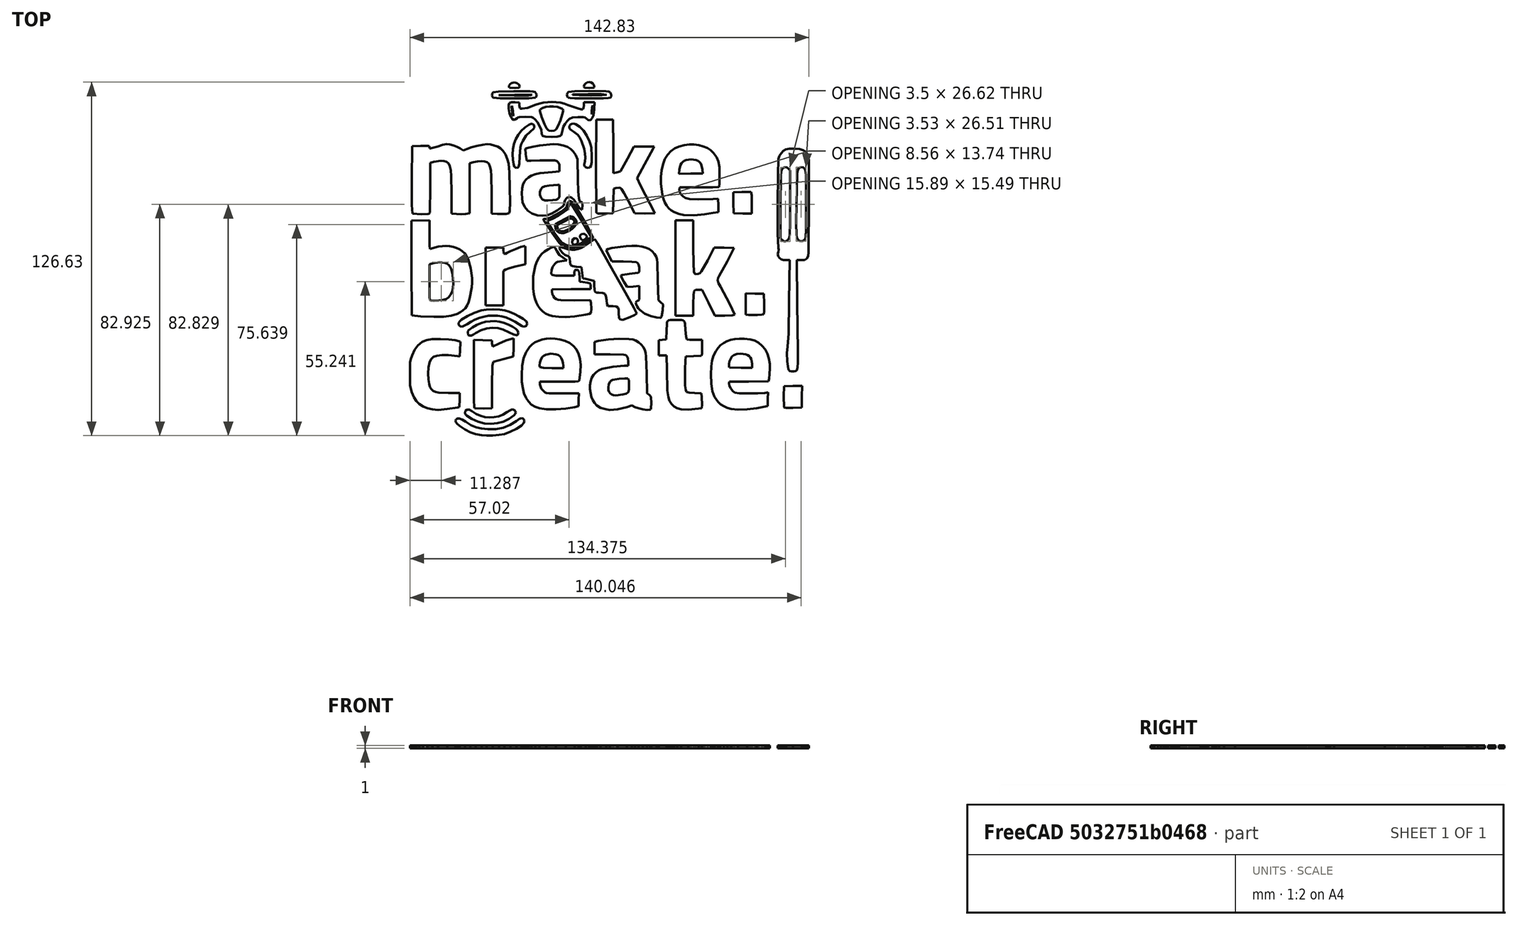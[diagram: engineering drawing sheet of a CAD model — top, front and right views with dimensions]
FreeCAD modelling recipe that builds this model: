
FCSTD DOCUMENT  (FreeCAD 1.0R39285 (Git))
Label: make_break_create_3d_01
License: All rights reserved
LicenseURL: http://www.ohwr.org/attachments/2388/cern_ohl_v_1_2.txt
objects: Part::Feature×50, Part::Extrusion×50, Part::Cut×12, Part::MultiFuse×2
note: 114 computed .brp shape members not serialized (recipe doc carries the construction recipe); baked Part::Feature solids carry a one-line shape summary decoded from their .brp

FEATURE [Part::Feature] Face
  shape: bbox 24.67 x 6.241 x 2e-07 mm, 1 faces, 0 solids (baked)
FEATURE [Part::Feature] Face001
  shape: bbox 18.26 x 5.149 x 2e-07 mm, 1 faces, 0 solids (baked)
FEATURE [Part::Feature] Face002
  shape: bbox 18.08 x 25.45 x 2e-07 mm, 1 faces, 0 solids (baked)
FEATURE [Part::Feature] Face003
  shape: bbox 21.9 x 25.59 x 2e-07 mm, 1 faces, 0 solids (baked)
FEATURE [Part::Feature] Face004
  shape: bbox 7.408 x 6.013 x 2e-07 mm, 1 faces, 0 solids (baked)
FEATURE [Part::Feature] Face005
  shape: bbox 21.11 x 25.45 x 2e-07 mm, 1 faces, 0 solids (baked)
FEATURE [Part::Feature] Face006
  shape: bbox 8.323 x 5.061 x 2e-07 mm, 1 faces, 0 solids (baked)
FEATURE [Part::Feature] Face007
  shape: bbox 15.61 x 32.1 x 2e-07 mm, 1 faces, 0 solids (baked)
FEATURE [Part::Feature] Face008
  shape: bbox 21.08 x 25.35 x 2e-07 mm, 1 faces, 0 solids (baked)
FEATURE [Part::Feature] Face009
  shape: bbox 8.448 x 5.165 x 2e-07 mm, 1 faces, 0 solids (baked)
FEATURE [Part::Feature] Face010
  shape: bbox 14.3 x 25.07 x 2e-07 mm, 1 faces, 0 solids (baked)
FEATURE [Part::Feature] Face011
  shape: bbox 6.571 x 7.896 x 2e-07 mm, 1 faces, 0 solids (baked)
FEATURE [Part::Feature] Face012
  shape: bbox 11.21 x 79.76 x 2e-07 mm, 1 faces, 0 solids (baked)
FEATURE [Part::Feature] Face013
  shape: bbox 3.498 x 26.62 x 2e-07 mm, 1 faces, 0 solids (baked)
FEATURE [Part::Feature] Face014
  shape: bbox 3.533 x 26.51 x 2e-07 mm, 1 faces, 0 solids (baked)
FEATURE [Part::Feature] Face015
  shape: bbox 17.99 x 5.158 x 2e-07 mm, 1 faces, 0 solids (baked)
FEATURE [Part::Feature] Face016
  shape: bbox 24.48 x 6.208 x 2e-07 mm, 1 faces, 0 solids (baked)
FEATURE [Part::Feature] Face017
  shape: bbox 27.63 x 28.88 x 2e-07 mm, 1 faces, 0 solids (baked)
FEATURE [Part::Feature] Face018
  shape: bbox 20.28 x 25.76 x 2e-07 mm, 1 faces, 0 solids (baked)
FEATURE [Part::Feature] Face019
  shape: bbox 21.72 x 34.62 x 2e-07 mm, 1 faces, 0 solids (baked)
FEATURE [Part::Feature] Face020
  shape: bbox 8.56 x 13.74 x 2e-07 mm, 1 faces, 0 solids (baked)
FEATURE [Part::Feature] Face021
  shape: bbox 20.87 x 25.1 x 2e-07 mm, 1 faces, 0 solids (baked)
FEATURE [Part::Feature] Face022
  shape: bbox 21.17 x 34.13 x 2e-07 mm, 1 faces, 0 solids (baked)
FEATURE [Part::Feature] Face023
  shape: bbox 6.556 x 7.79 x 2e-07 mm, 1 faces, 0 solids (baked)
FEATURE [Part::Feature] Face024
  shape: bbox 14.23 x 21.17 x 2e-07 mm, 1 faces, 0 solids (baked)
FEATURE [Part::Feature] Face025
  shape: bbox 17.77 x 16.59 x 2e-07 mm, 1 faces, 0 solids (baked)
FEATURE [Part::Feature] Face026
  shape: bbox 15.89 x 15.49 x 2e-07 mm, 1 faces, 0 solids (baked)
FEATURE [Part::Feature] Face027
  shape: bbox 2.125 x 2.325 x 2e-07 mm, 1 faces, 0 solids (baked)
FEATURE [Part::Feature] Face028
  shape: bbox 2.507 x 2.314 x 2e-07 mm, 1 faces, 0 solids (baked)
FEATURE [Part::Feature] Face029
  shape: bbox 7.664 x 6.077 x 2e-07 mm, 1 faces, 0 solids (baked)
FEATURE [Part::Feature] Face030
  shape: bbox 6.04 x 4.588 x 2e-07 mm, 1 faces, 0 solids (baked)
FEATURE [Part::Feature] Face031
  shape: bbox 21.68 x 25.65 x 2e-07 mm, 1 faces, 0 solids (baked)
FEATURE [Part::Feature] Face032
  shape: bbox 7.013 x 5.604 x 2e-07 mm, 1 faces, 0 solids (baked)
FEATURE [Part::Feature] Face033
  shape: bbox 20.97 x 25.39 x 2e-07 mm, 1 faces, 0 solids (baked)
FEATURE [Part::Feature] Face034
  shape: bbox 8.401 x 5.128 x 2e-07 mm, 1 faces, 0 solids (baked)
FEATURE [Part::Feature] Face035
  shape: bbox 35.11 x 25.08 x 2e-07 mm, 1 faces, 0 solids (baked)
FEATURE [Part::Feature] Face036
  shape: bbox 21.11 x 33.68 x 2e-07 mm, 1 faces, 0 solids (baked)
FEATURE [Part::Feature] Face037
  shape: bbox 6.615 x 7.752 x 2e-07 mm, 1 faces, 0 solids (baked)
FEATURE [Part::Feature] Face038
  shape: bbox 7.78 x 15.77 x 2e-07 mm, 1 faces, 0 solids (baked)
FEATURE [Part::Feature] Face039
  shape: bbox 7.999 x 15.82 x 2e-07 mm, 1 faces, 0 solids (baked)
FEATURE [Part::Feature] Face040
  shape: bbox 30.72 x 12.5 x 2e-07 mm, 1 faces, 0 solids (baked)
FEATURE [Part::Feature] Face041
  shape: bbox 8.329 x 8.723 x 2e-07 mm, 1 faces, 0 solids (baked)
FEATURE [Part::Feature] Face042
  shape: bbox 0.6332 x 3.652 x 2e-07 mm, 1 faces, 0 solids (baked)
FEATURE [Part::Feature] Face043
  shape: bbox 0.3788 x 3.244 x 2e-07 mm, 1 faces, 0 solids (baked)
FEATURE [Part::Feature] Face044
  shape: bbox 15.91 x 2.597 x 2e-07 mm, 1 faces, 0 solids (baked)
FEATURE [Part::Feature] Face045
  shape: bbox 11.85 x 0.339 x 2e-07 mm, 1 faces, 0 solids (baked)
FEATURE [Part::Feature] Face046
  shape: bbox 15.85 x 2.668 x 2e-07 mm, 1 faces, 0 solids (baked)
FEATURE [Part::Feature] Face047
  shape: bbox 12.2 x 0.4689 x 2e-07 mm, 1 faces, 0 solids (baked)
FEATURE [Part::Feature] Face048
  shape: bbox 3.826 x 1.977 x 2e-07 mm, 1 faces, 0 solids (baked)
FEATURE [Part::Feature] Face049
  shape: bbox 3.704 x 2.117 x 2e-07 mm, 1 faces, 0 solids (baked)
FEATURE [Part::Extrusion] Extrude
  Base = -> Face
  Dir = (0,0,-1)
  DirMode = 2
  FaceMakerClass = Part::FaceMakerBullseye
  FaceMakerMode = 3
  LengthFwd = 1
  LengthRev = 0
  Solid = false
  Symmetric = false
FEATURE [Part::Extrusion] Extrude001
  Base = -> Face001
  Dir = (0,0,-1)
  DirMode = 2
  FaceMakerClass = Part::FaceMakerBullseye
  FaceMakerMode = 3
  LengthFwd = 1
  LengthRev = 0
  Solid = false
  Symmetric = false
FEATURE [Part::Extrusion] Extrude002
  Base = -> Face002
  Dir = (0,0,-1)
  DirMode = 2
  FaceMakerClass = Part::FaceMakerBullseye
  FaceMakerMode = 3
  LengthFwd = 1
  LengthRev = 0
  Solid = false
  Symmetric = false
FEATURE [Part::Extrusion] Extrude003
  Base = -> Face003
  Dir = (0,0,-1)
  DirMode = 2
  FaceMakerClass = Part::FaceMakerBullseye
  FaceMakerMode = 3
  LengthFwd = 1
  LengthRev = 0
  Solid = false
  Symmetric = false
FEATURE [Part::Extrusion] Extrude004
  Base = -> Face004
  Dir = (0,0,1)
  DirMode = 2
  FaceMakerClass = Part::FaceMakerBullseye
  FaceMakerMode = 3
  LengthFwd = -1
  LengthRev = 0
  Solid = false
  Symmetric = false
FEATURE [Part::Extrusion] Extrude005
  Base = -> Face005
  Dir = (0,0,-1)
  DirMode = 2
  FaceMakerClass = Part::FaceMakerBullseye
  FaceMakerMode = 3
  LengthFwd = 1
  LengthRev = 0
  Solid = false
  Symmetric = false
FEATURE [Part::Extrusion] Extrude006
  Base = -> Face006
  Dir = (0,0,1)
  DirMode = 2
  FaceMakerClass = Part::FaceMakerBullseye
  FaceMakerMode = 3
  LengthFwd = -1
  LengthRev = 0
  Solid = false
  Symmetric = false
FEATURE [Part::Extrusion] Extrude007
  Base = -> Face007
  Dir = (0,0,-1)
  DirMode = 2
  FaceMakerClass = Part::FaceMakerBullseye
  FaceMakerMode = 3
  LengthFwd = 1
  LengthRev = 0
  Solid = false
  Symmetric = false
FEATURE [Part::Extrusion] Extrude008
  Base = -> Face008
  Dir = (0,0,-1)
  DirMode = 2
  FaceMakerClass = Part::FaceMakerBullseye
  FaceMakerMode = 3
  LengthFwd = 1
  LengthRev = 0
  Solid = false
  Symmetric = false
FEATURE [Part::Extrusion] Extrude009
  Base = -> Face009
  Dir = (0,0,1)
  DirMode = 2
  FaceMakerClass = Part::FaceMakerBullseye
  FaceMakerMode = 3
  LengthFwd = -1
  LengthRev = 0
  Solid = false
  Symmetric = false
FEATURE [Part::Extrusion] Extrude010
  Base = -> Face010
  Dir = (0,0,-1)
  DirMode = 2
  FaceMakerClass = Part::FaceMakerBullseye
  FaceMakerMode = 3
  LengthFwd = 1
  LengthRev = 0
  Solid = false
  Symmetric = false
FEATURE [Part::Extrusion] Extrude011
  Base = -> Face011
  Dir = (0,0,-1)
  DirMode = 2
  FaceMakerClass = Part::FaceMakerBullseye
  FaceMakerMode = 3
  LengthFwd = 1
  LengthRev = 0
  Solid = false
  Symmetric = false
FEATURE [Part::Extrusion] Extrude012
  Base = -> Face012
  Dir = (0,0,-1)
  DirMode = 2
  FaceMakerClass = Part::FaceMakerBullseye
  FaceMakerMode = 3
  LengthFwd = 1
  LengthRev = 0
  Solid = false
  Symmetric = false
FEATURE [Part::Extrusion] Extrude013
  Base = -> Face013
  Dir = (0,0,1)
  DirMode = 2
  FaceMakerClass = Part::FaceMakerBullseye
  FaceMakerMode = 3
  LengthFwd = -1
  LengthRev = 0
  Solid = false
  Symmetric = false
FEATURE [Part::Extrusion] Extrude014
  Base = -> Face014
  Dir = (0,0,1)
  DirMode = 2
  FaceMakerClass = Part::FaceMakerBullseye
  FaceMakerMode = 3
  LengthFwd = -1
  LengthRev = 0
  Solid = false
  Symmetric = false
FEATURE [Part::Extrusion] Extrude015
  Base = -> Face015
  Dir = (0,0,-1)
  DirMode = 2
  FaceMakerClass = Part::FaceMakerBullseye
  FaceMakerMode = 3
  LengthFwd = 1
  LengthRev = 0
  Solid = false
  Symmetric = false
FEATURE [Part::Extrusion] Extrude016
  Base = -> Face016
  Dir = (0,0,-1)
  DirMode = 2
  FaceMakerClass = Part::FaceMakerBullseye
  FaceMakerMode = 3
  LengthFwd = 1
  LengthRev = 0
  Solid = false
  Symmetric = false
FEATURE [Part::Extrusion] Extrude017
  Base = -> Face017
  Dir = (0,0,-1)
  DirMode = 2
  FaceMakerClass = Part::FaceMakerBullseye
  FaceMakerMode = 3
  LengthFwd = 1
  LengthRev = 0
  Solid = false
  Symmetric = false
FEATURE [Part::Extrusion] Extrude018
  Base = -> Face018
  Dir = (0,0,-1)
  DirMode = 2
  FaceMakerClass = Part::FaceMakerBullseye
  FaceMakerMode = 3
  LengthFwd = 1
  LengthRev = 0
  Solid = false
  Symmetric = false
FEATURE [Part::Extrusion] Extrude019
  Base = -> Face019
  Dir = (0,0,-1)
  DirMode = 2
  FaceMakerClass = Part::FaceMakerBullseye
  FaceMakerMode = 3
  LengthFwd = 1
  LengthRev = 0
  Solid = false
  Symmetric = false
FEATURE [Part::Extrusion] Extrude020
  Base = -> Face020
  Dir = (0,0,1)
  DirMode = 2
  FaceMakerClass = Part::FaceMakerBullseye
  FaceMakerMode = 3
  LengthFwd = -1
  LengthRev = 0
  Solid = false
  Symmetric = false
FEATURE [Part::Extrusion] Extrude021
  Base = -> Face021
  Dir = (0,0,-1)
  DirMode = 2
  FaceMakerClass = Part::FaceMakerBullseye
  FaceMakerMode = 3
  LengthFwd = 1
  LengthRev = 0
  Solid = false
  Symmetric = false
FEATURE [Part::Extrusion] Extrude022
  Base = -> Face022
  Dir = (0,0,-1)
  DirMode = 2
  FaceMakerClass = Part::FaceMakerBullseye
  FaceMakerMode = 3
  LengthFwd = 1
  LengthRev = 0
  Solid = false
  Symmetric = false
FEATURE [Part::Extrusion] Extrude023
  Base = -> Face023
  Dir = (0,0,-1)
  DirMode = 2
  FaceMakerClass = Part::FaceMakerBullseye
  FaceMakerMode = 3
  LengthFwd = 1
  LengthRev = 0
  Solid = false
  Symmetric = false
FEATURE [Part::Extrusion] Extrude024
  Base = -> Face024
  Dir = (0,0,-1)
  DirMode = 2
  FaceMakerClass = Part::FaceMakerBullseye
  FaceMakerMode = 3
  LengthFwd = 1
  LengthRev = 0
  Solid = false
  Symmetric = false
FEATURE [Part::Extrusion] Extrude025
  Base = -> Face025
  Dir = (0,0,-1)
  DirMode = 2
  FaceMakerClass = Part::FaceMakerBullseye
  FaceMakerMode = 3
  LengthFwd = 1
  LengthRev = 0
  Solid = false
  Symmetric = false
FEATURE [Part::Extrusion] Extrude026
  Base = -> Face026
  Dir = (0,0,1)
  DirMode = 2
  FaceMakerClass = Part::FaceMakerBullseye
  FaceMakerMode = 3
  LengthFwd = -1
  LengthRev = 0
  Solid = false
  Symmetric = false
FEATURE [Part::Extrusion] Extrude027
  Base = -> Face027
  Dir = (0,0,-1)
  DirMode = 2
  FaceMakerClass = Part::FaceMakerBullseye
  FaceMakerMode = 3
  LengthFwd = 1
  LengthRev = 0
  Solid = false
  Symmetric = false
FEATURE [Part::Extrusion] Extrude028
  Base = -> Face028
  Dir = (0,0,-1)
  DirMode = 2
  FaceMakerClass = Part::FaceMakerBullseye
  FaceMakerMode = 3
  LengthFwd = 1
  LengthRev = 0
  Solid = false
  Symmetric = false
FEATURE [Part::Extrusion] Extrude029
  Base = -> Face029
  Dir = (0,0,-1)
  DirMode = 2
  FaceMakerClass = Part::FaceMakerBullseye
  FaceMakerMode = 3
  LengthFwd = 1
  LengthRev = 0
  Solid = false
  Symmetric = false
FEATURE [Part::Extrusion] Extrude030
  Base = -> Face030
  Dir = (0,0,1)
  DirMode = 2
  FaceMakerClass = Part::FaceMakerBullseye
  FaceMakerMode = 3
  LengthFwd = -1
  LengthRev = 0
  Solid = false
  Symmetric = false
FEATURE [Part::Extrusion] Extrude031
  Base = -> Face031
  Dir = (0,0,-1)
  DirMode = 2
  FaceMakerClass = Part::FaceMakerBullseye
  FaceMakerMode = 3
  LengthFwd = 1
  LengthRev = 0
  Solid = false
  Symmetric = false
FEATURE [Part::Extrusion] Extrude032
  Base = -> Face032
  Dir = (0,0,1)
  DirMode = 2
  FaceMakerClass = Part::FaceMakerBullseye
  FaceMakerMode = 3
  LengthFwd = -1
  LengthRev = 0
  Solid = false
  Symmetric = false
FEATURE [Part::Extrusion] Extrude033
  Base = -> Face033
  Dir = (0,0,-1)
  DirMode = 2
  FaceMakerClass = Part::FaceMakerBullseye
  FaceMakerMode = 3
  LengthFwd = 1
  LengthRev = 0
  Solid = false
  Symmetric = false
FEATURE [Part::Extrusion] Extrude034
  Base = -> Face034
  Dir = (0,0,1)
  DirMode = 2
  FaceMakerClass = Part::FaceMakerBullseye
  FaceMakerMode = 3
  LengthFwd = -1
  LengthRev = 0
  Solid = false
  Symmetric = false
FEATURE [Part::Extrusion] Extrude035
  Base = -> Face035
  Dir = (0,0,-1)
  DirMode = 2
  FaceMakerClass = Part::FaceMakerBullseye
  FaceMakerMode = 3
  LengthFwd = 1
  LengthRev = 0
  Solid = false
  Symmetric = false
FEATURE [Part::Extrusion] Extrude036
  Base = -> Face036
  Dir = (0,0,-1)
  DirMode = 2
  FaceMakerClass = Part::FaceMakerBullseye
  FaceMakerMode = 3
  LengthFwd = 1
  LengthRev = 0
  Solid = false
  Symmetric = false
FEATURE [Part::Extrusion] Extrude037
  Base = -> Face037
  Dir = (0,0,-1)
  DirMode = 2
  FaceMakerClass = Part::FaceMakerBullseye
  FaceMakerMode = 3
  LengthFwd = 1
  LengthRev = 0
  Solid = false
  Symmetric = false
FEATURE [Part::Extrusion] Extrude038
  Base = -> Face038
  Dir = (0,0,-1)
  DirMode = 2
  FaceMakerClass = Part::FaceMakerBullseye
  FaceMakerMode = 3
  LengthFwd = 1
  LengthRev = 0
  Solid = false
  Symmetric = false
FEATURE [Part::Extrusion] Extrude039
  Base = -> Face039
  Dir = (0,0,-1)
  DirMode = 2
  FaceMakerClass = Part::FaceMakerBullseye
  FaceMakerMode = 3
  LengthFwd = 1
  LengthRev = 0
  Solid = false
  Symmetric = false
FEATURE [Part::Extrusion] Extrude040
  Base = -> Face040
  Dir = (0,0,-1)
  DirMode = 2
  FaceMakerClass = Part::FaceMakerBullseye
  FaceMakerMode = 3
  LengthFwd = 1
  LengthRev = 0
  Solid = false
  Symmetric = false
FEATURE [Part::Extrusion] Extrude041
  Base = -> Face041
  Dir = (0,0,1)
  DirMode = 2
  FaceMakerClass = Part::FaceMakerBullseye
  FaceMakerMode = 3
  LengthFwd = -1
  LengthRev = 0
  Solid = false
  Symmetric = false
FEATURE [Part::Extrusion] Extrude042
  Base = -> Face042
  Dir = (0,0,1)
  DirMode = 2
  FaceMakerClass = Part::FaceMakerBullseye
  FaceMakerMode = 3
  LengthFwd = -1
  LengthRev = 0
  Solid = false
  Symmetric = false
FEATURE [Part::Extrusion] Extrude043
  Base = -> Face043
  Dir = (0,0,1)
  DirMode = 2
  FaceMakerClass = Part::FaceMakerBullseye
  FaceMakerMode = 3
  LengthFwd = -1
  LengthRev = 0
  Solid = false
  Symmetric = false
FEATURE [Part::Extrusion] Extrude044
  Base = -> Face044
  Dir = (0,0,-1)
  DirMode = 2
  FaceMakerClass = Part::FaceMakerBullseye
  FaceMakerMode = 3
  LengthFwd = 1
  LengthRev = 0
  Solid = false
  Symmetric = false
FEATURE [Part::Extrusion] Extrude045
  Base = -> Face045
  Dir = (0,0,1)
  DirMode = 2
  FaceMakerClass = Part::FaceMakerBullseye
  FaceMakerMode = 3
  LengthFwd = -1
  LengthRev = 0
  Solid = false
  Symmetric = false
FEATURE [Part::Extrusion] Extrude046
  Base = -> Face046
  Dir = (0,0,-1)
  DirMode = 2
  FaceMakerClass = Part::FaceMakerBullseye
  FaceMakerMode = 3
  LengthFwd = 1
  LengthRev = 0
  Solid = false
  Symmetric = false
FEATURE [Part::Extrusion] Extrude047
  Base = -> Face047
  Dir = (0,0,1)
  DirMode = 2
  FaceMakerClass = Part::FaceMakerBullseye
  FaceMakerMode = 3
  LengthFwd = -1
  LengthRev = 0
  Solid = false
  Symmetric = false
FEATURE [Part::Extrusion] Extrude048
  Base = -> Face048
  Dir = (0,0,-1)
  DirMode = 2
  FaceMakerClass = Part::FaceMakerBullseye
  FaceMakerMode = 3
  LengthFwd = 1
  LengthRev = 0
  Solid = false
  Symmetric = false
FEATURE [Part::Extrusion] Extrude049
  Base = -> Face049
  Dir = (0,0,-1)
  DirMode = 2
  FaceMakerClass = Part::FaceMakerBullseye
  FaceMakerMode = 3
  LengthFwd = 1
  LengthRev = 0
  Solid = false
  Symmetric = false
FEATURE [Part::Cut] Cut
  Base = -> Extrude003
  Refine = true
  Tool = -> Extrude004
FEATURE [Part::Cut] Cut001
  Base = -> Extrude005
  Refine = true
  Tool = -> Extrude006
FEATURE [Part::Cut] Cut002
  Base = -> Extrude008
  Refine = true
  Tool = -> Extrude009
FEATURE [Part::MultiFuse] Fusion
  Refine = true
  Shapes = -> [Extrude013,Extrude014]
FEATURE [Part::Cut] Cut003
  Base = -> Extrude012
  Refine = true
  Tool = -> Fusion
FEATURE [Part::Cut] Cut004
  Base = -> Extrude019
  Refine = true
  Tool = -> Extrude020
FEATURE [Part::Cut] Cut005
  Base = -> Extrude031
  Refine = true
  Tool = -> Extrude032
FEATURE [Part::Cut] Cut006
  Base = -> Extrude033
  Refine = true
  Tool = -> Extrude034
FEATURE [Part::MultiFuse] Fusion001
  Refine = true
  Shapes = -> [Extrude041,Extrude042,Extrude043]
FEATURE [Part::Cut] Cut007
  Base = -> Extrude040
  Refine = true
  Tool = -> Fusion001
FEATURE [Part::Cut] Cut008
  Base = -> Extrude044
  Refine = true
  Tool = -> Extrude045
FEATURE [Part::Cut] Cut009
  Base = -> Extrude046
  Refine = true
  Tool = -> Extrude047
FEATURE [Part::Cut] Cut010
  Base = -> Extrude025
  Refine = true
  Tool = -> Extrude026
FEATURE [Part::Cut] Cut011
  Base = -> Extrude029
  Refine = true
  Tool = -> Extrude030
